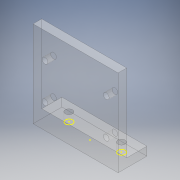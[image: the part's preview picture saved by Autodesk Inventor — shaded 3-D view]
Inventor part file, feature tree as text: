
AUTODESK INVENTOR PART (.ipt)
format: ipt  version: 2017 (Build 210142000, 142)  size: 159,232 bytes
history: native  units: mm
features: sketch x6, extrude x5
ambient origin geometry x8: Origin, YZ Plane, XZ Plane, XY Plane, X Axis, Y Axis, Z Axis, Center Point
bodies: Body1 (feature_tree)
feature tree (11):
  extrude  "Extrusion4"  Depth=10.0mm
  extrude  "Extrusion5"  Depth=2.5mm
  sketch  "Sketch4"  dims[d18=3.0mm d19=0.0mm d24=3.0mm]
  extrude  "Extrusion7"  Depth=3.0mm
  sketch  "Sketch5"  dims[d25=27.0mm d26=0.0mm d50=3.0mm d51=0.0mm]
  extrude  "Extrusion8"  Depth=3.0mm TaperAngle=0.0deg
  extrude  "Extrusion9"  Depth=8.0mm
  sketch  "Sketch1"  dims[d0=24.0mm d1=10.0mm]
  sketch  "Sketch3"  dims[d14=2.5mm d15=2.5mm]
  sketch  "Sketch6"  dims[d55=8.0mm d58=8.0mm]
  sketch  "Sketch7"  dims[d60=1.625mm d61=1.625mm d62=18.250508mm d63=2.75mm d64=0.0mm d65=2.75mm d66=0.0mm d68=1.375mm d69=1.375mm d70=1.375mm d71=1.375mm]
